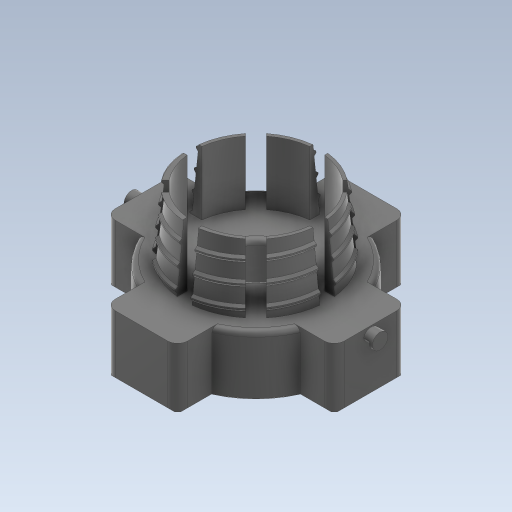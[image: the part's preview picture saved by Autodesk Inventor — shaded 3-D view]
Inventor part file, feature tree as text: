
AUTODESK INVENTOR PART (.ipt)
format: ipt  version: 2023 (Build 270158000, 158)  size: 1,052,672 bytes
history: native  units: mm
features: sketch x7, extrude x6, fillet x3, other x2, helix x2, draft x1, direct_edit x1, hole x1, pattern_circular x1, chamfer x1, projected_geometry x1
ambient origin geometry x8: Origin, YZ Plane, XZ Plane, XY Plane, X Axis, Y Axis, Z Axis, Center Point
bodies: Solid1 (feature_tree)
feature tree (26):
  other  "Slider V8 (4mm pitch)"
  extrude  "Extrusion1"  Depth=26.5mm
  draft  "FaceDraft1"
  sketch  "Sketch2"  dims[d34=0.0mm d35=0.0mm]
  helix  "Coil3"  [1 undecoded]
  helix  "Coil4"  [1 undecoded]
  direct_edit  "Direct Edit2"
  extrude  "Extrusion2"  Depth=12.0mm TaperAngle=0.0deg
  sketch  "Sketch4"  dims[d56=8.726646mm d62=4.0mm d63=13.0mm d64=10.0mm d65=1.047198mm]
  extrude  "Extrusion3"  Depth=10.0mm
  extrude  "Extrusion8"  TaperAngle=90.0deg  [1 undecoded]
  hole  "Hole1"  [1 undecoded]
  sketch  "Sketch9"  dims[d83=3.0mm d84=1.5mm d85=1.5mm d86=0.0mm d87=0.0mm d91=3.0mm d92=3.0mm d93=1.5mm d94=1.5mm d95=5.3mm d96=6.0mm d97=10.0mm d98=10.0mm d99=90.0deg d100=8.0mm d101=20.594885mm d108=35.6mm d110=3.15mm d113=1.575mm d114=7.45mm d115=2.35mm d117=3.6mm d118=0.0mm d119=1.2mm d120=0.0mm d121=20.0mm d122=360.0deg d126=1.0mm d129=0.3mm d130=2.0mm d131=45.0deg d133=14.65mm d134=14.65mm d137=23.15mm d138=46.3mm d139=46.3mm d142=1.0mm d143=2.0mm d109=0.5mm d111=0.5mm d112=0.872665mm]
  extrude  "Extrusion11"  Depth=2.0mm
  extrude  "Extrusion12"  Depth=2.0mm
  pattern_circular  "Circular Pattern1"  [2 undecoded]
  fillet  "Fillet4"  Radius=3.0mm
  chamfer  "Chamfer2"  Distance=3.0mm
  fillet  "Fillet7"  Radius=1.5mm
  fillet  "Fillet8"  Radius=1.5mm
  sketch  "Sketch1"  dims[d0=25.0mm d1=26.5mm d2=12.875mm d3=0.0mm d4=1.047198mm]
  sketch  "Sketch3"  dims[d36=7.325mm d37=7.0mm d38=7.325mm d39=0.0mm d40=7.0mm d41=28.73603mm d42=12.0mm d43=0.0mm]
  sketch  "Sketch5"  dims[d66=90.0deg d67=90.0deg d68=0.0mm d69=0.0mm d70=4.0mm d71=3.0mm d72=10.0mm d73=-1.047198mm d74=90.0deg d75=90.0deg d76=0.0mm d77=0.0mm]
  sketch  "Sketch7"  dims[d79=-0.127mm d82=3.0mm]
  projected_geometry  "Projected Loop1"
  other  "Size2"
note: 6 required parameter values undecoded (feature->parameter linkage not recoverable at this tier; creation-order binding heuristic only, values carry confidence <= 0.55)
